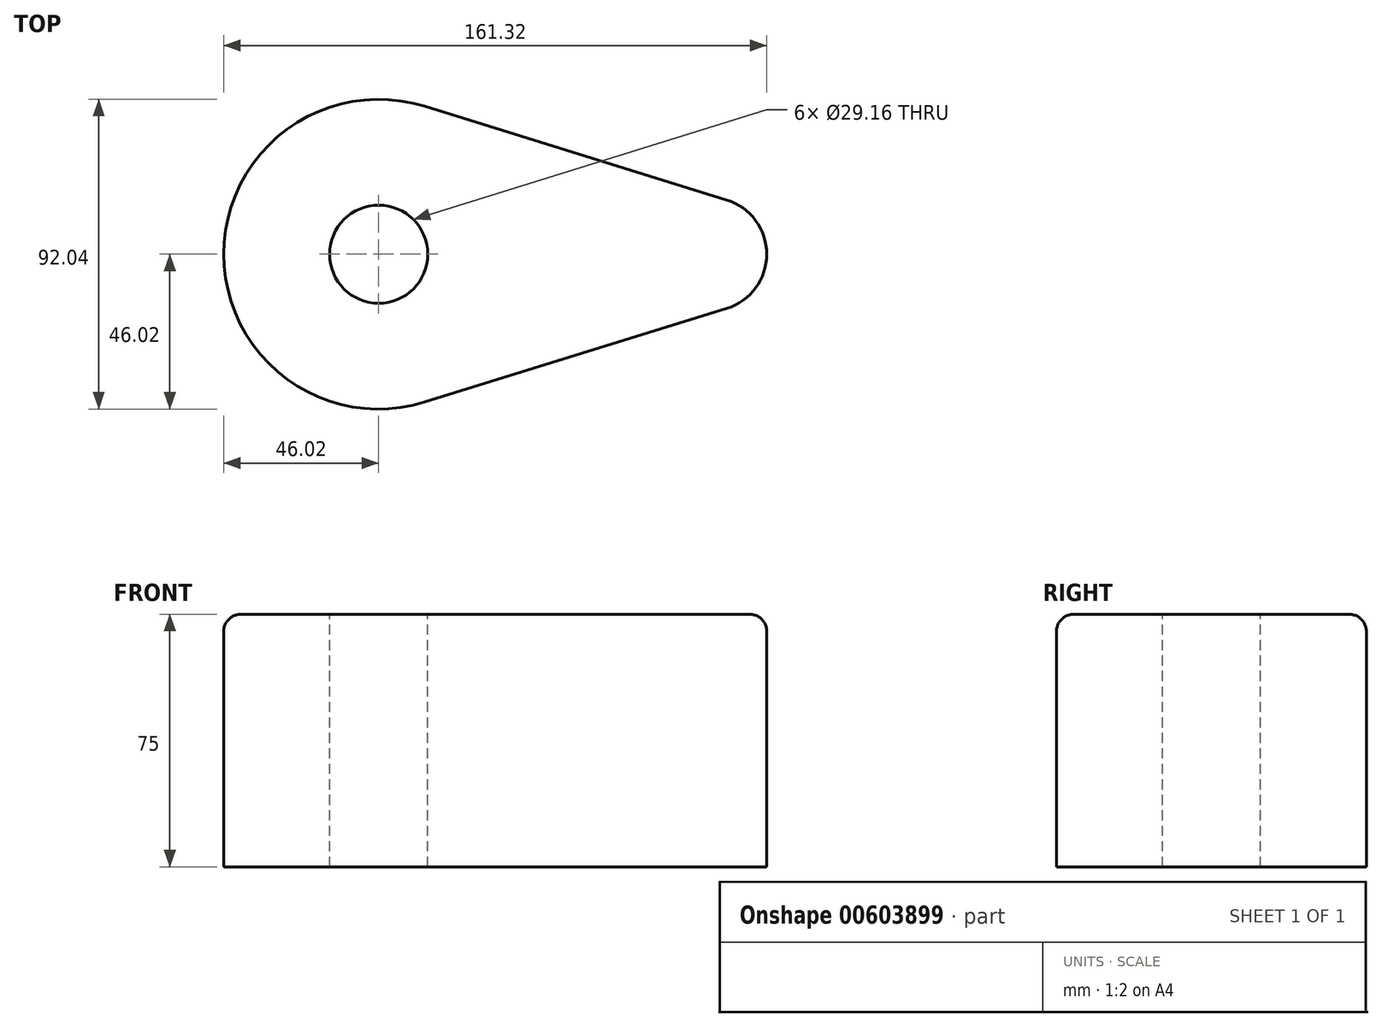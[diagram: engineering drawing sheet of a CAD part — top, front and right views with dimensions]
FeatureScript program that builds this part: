
annotation { "Feature Type Name" : "Feature", "Feature Type Description" : "" }
export const myFeature = defineFeature(function(context is Context, id is Id, definition is map)
    precondition{}
    {
        {
            var Q0;
            Q0=qCreatedBy(makeId("Top.planeOp"),FACE);
            var sketch = newSketch(context, id + "F0", { "sketchPlane" : qUnion([Q0])});
            skCircle(sketch, "E0", {"center": v(0, 0) * mm, "radius": 46.02 * mm});
            skCircle(sketch, "E1", {"center": v(98.44, 0) * mm, "radius": 16.86 * mm});
            skLineSegment(sketch, "E2", {"start": v(13.63, 43.95) * mm, "end": v(103.43, 16.1) * mm});
            skLineSegment(sketch, "E3", {"start": v(13.63, -43.95) * mm, "end": v(103.43, -16.1) * mm});
            skSolve(sketch);
        }
        {
            var Q0;
            Q0 = qSketchRegion(id + "F0", true);
            extrude(context, id + "F1", {"entities" : qUnion([Q0]), "endBound" : BoundingType.SYMMETRIC, "depth" : 75 * mm, "offsetDistance" : 25 * mm});
        }
        {
            var Q0;
            Q0=qCreatedBy(makeId("Top.planeOp"),FACE);
            var sketch = newSketch(context, id + "F2", { "sketchPlane" : qUnion([Q0])});
            skCircle(sketch, "E4", {"center": v(0, 0) * mm, "radius": 14.58 * mm});
            skSolve(sketch);
        }
        {
            var Q0;
            Q0 = qSketchRegion(id + "F2", true);
            extrude(context, id + "F3", {"entities" : qUnion([Q0]), "operationType" : NewBodyOperationType.REMOVE, "endBound" : BoundingType.THROUGH_ALL, "oppositeDirection" : true, "depth" : 25 * mm, "offsetDistance" : 25 * mm, "hasSecondDirection" : true, "secondDirectionBound" : SecondDirectionBoundingType.THROUGH_ALL, "secondDirectionOppositeDirection" : false, "secondDirectionDepth" : 25 * mm});
        }
        {
            var Q0;
            Q0=makeQuery(id+"F1.opExtrude","CAP_EDGE",EDGE,{"disambiguationData":[OSD([sQuery(id+"F0.wireOp",EDGE,"E3")])],"isStart":false});
            fillet(context, id + "F4", {"entities" : qUnion([Q0]), "radius" : 5 * mm, "tangentPropagation" : true, "allowEdgeOverflow" : false});
        }
    });
